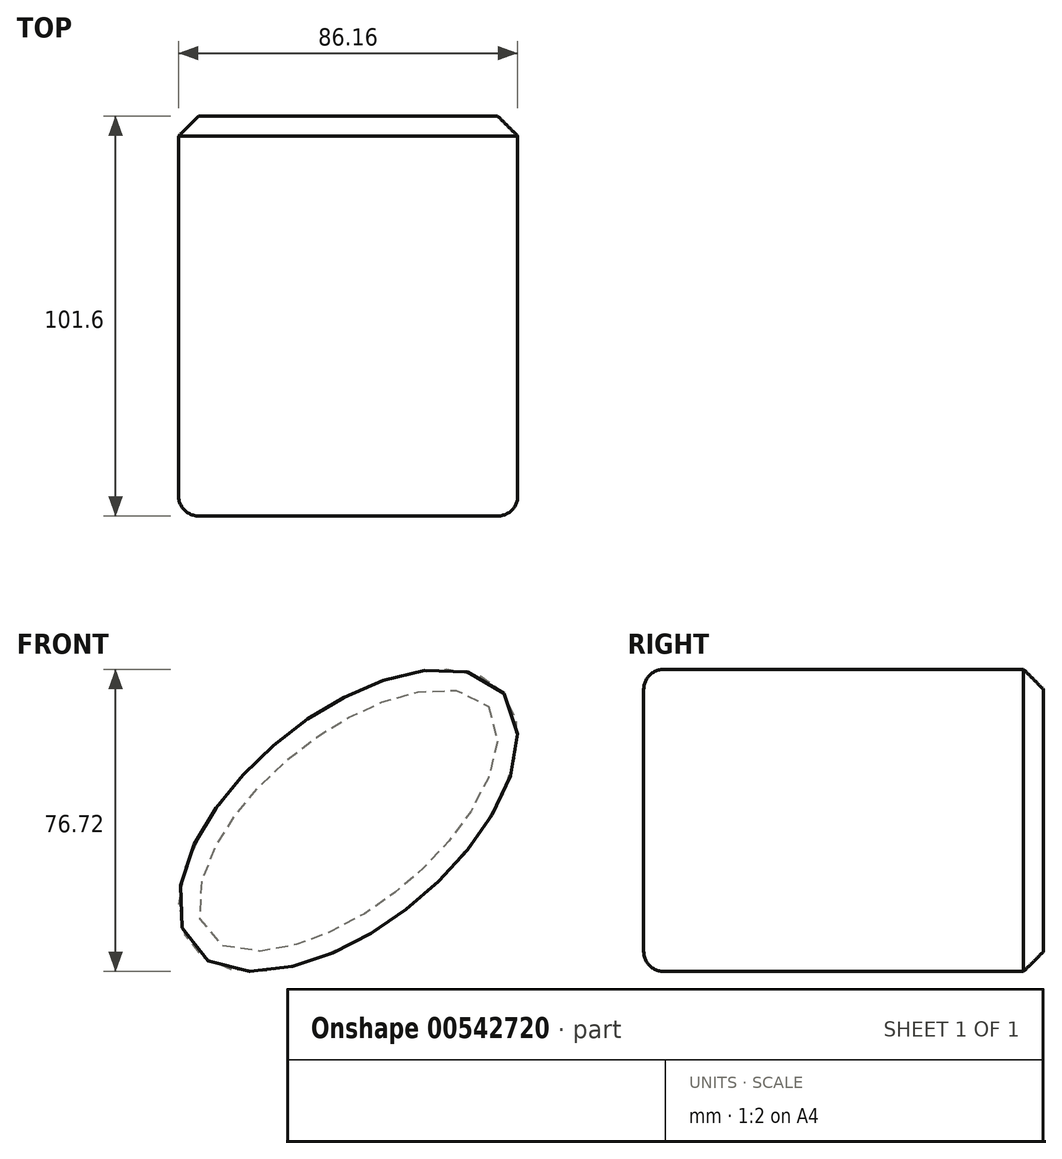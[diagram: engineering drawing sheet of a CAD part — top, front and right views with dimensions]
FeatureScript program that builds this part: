
annotation { "Feature Type Name" : "Feature", "Feature Type Description" : "" }
export const myFeature = defineFeature(function(context is Context, id is Id, definition is map)
    precondition{}
    {
        {
            var Q0;
            Q0=qCreatedBy(makeId("Front.planeOp"),FACE);
            var sketch = newSketch(context, id + "F0", { "sketchPlane" : qUnion([Q0])});
            skEllipse(sketch, "E0", {"center": v(0, 0) * mm, "majorRadius": 51.06 * mm, "minorRadius": 26.84 * mm, "majorAxis": v(0.78, 0.63)});
            skSolve(sketch);
        }
        {
            var Q0;
            Q0=makeQuery(id+"F0.imprint","IMPRINT",FACE,{"disambiguationData":[TD([[makeQuery(id+"F0.imprint","IMPRINT",EDGE,{"derivedFrom":sQuery(id+"F0.wireOp",EDGE,"E0")}),1.0]])]});
            extrude(context, id + "F1", {"entities" : qUnion([Q0]), "depth" : 101.6 * mm, "offsetDistance" : 25.4 * mm});
        }
        {
            var Q0;
            Q0=makeQuery(id+"F1.opExtrude","CAP_EDGE",EDGE,{"disambiguationData":[OSD([sQuery(id+"F0.wireOp",EDGE,"E0")])],"isStart":true});
            chamfer(context, id + "F2", {"entities" : qUnion([Q0]), "width" : 5.08 * mm, "tangentPropagation" : true});
        }
        {
            var Q0;
            Q0=makeQuery(id+"F1.opExtrude","CAP_EDGE",EDGE,{"disambiguationData":[OSD([sQuery(id+"F0.wireOp",EDGE,"E0")])],"isStart":false});
            fillet(context, id + "F3", {"entities" : qUnion([Q0]), "radius" : 5.08 * mm, "tangentPropagation" : true, "allowEdgeOverflow" : false});
        }
    });
